# Revit family: 977210001_Llave jardin cromada
name_source: partatom
category: Plumbing Fixtures
units: mm (PartAtom-declared; Revit-internal decimal feet)

## family parameters
Always vertical = Yes
Cut with Voids When Loaded = No
OmniClass Number = 23.31.11.00
OmniClass Title = Faucets
Part Type = Normal
Room Calculation Point = No
Round Connector Dimension = Use Diameter
Shared = No
Work Plane-Based = No

## types (2) — shared parameters
Alto = 75 mm
Ancho = 59 mm
Capacidad de flujo = A 20 psi: 27.6 L/min.
Ciclo de vida de la unidad de cierre = 500000 ciclos.
Creado por = BIMBAU
Description = La grifería llave jardín ha sido diseñada para trabjar en perfecta armonía con el espacio; inspirada en las necesidades del consumidor latinoamericano dando como resultado un producto robusto y funcional.
Dimensiones generales del producto = 79 x 59 x 101 mm.
Diámetro abasto = 13 mm
Fecha de creación = 11/05/2021
Garantía = 5 años Grival.
Manufacturer = Corona.
Material = Corona_Cromado
Material 2 = Corona_Acabado_Satinado
Model = 977263331_Llave jardin cromada.
Normatividad = NTC 1644.
Peso  Bruto = 200 g. - 0.44 lb.
Peso neto = 180 g. - 0.40 lb.
Presión máxima recomendada = 125 psi.
Presión mínima recomendada = 20 psi.
Profundidad = 101 mm
Temperaturas máxima de trabajo = 71° C - 159.8° F.
Temperaturas mínima de trabajo = 5° C - 41° F.
zero-valued in all types: Default Elevation

## per-type parameters (varying)
| type | Cromo | Satin |
| Llave jardín cromada | Yes | No |
| Llave jardin satinada | No | Yes |

## geometry (parser evidence)
native form markers: Sweep x2
no freeform markers — native parametric forms only
